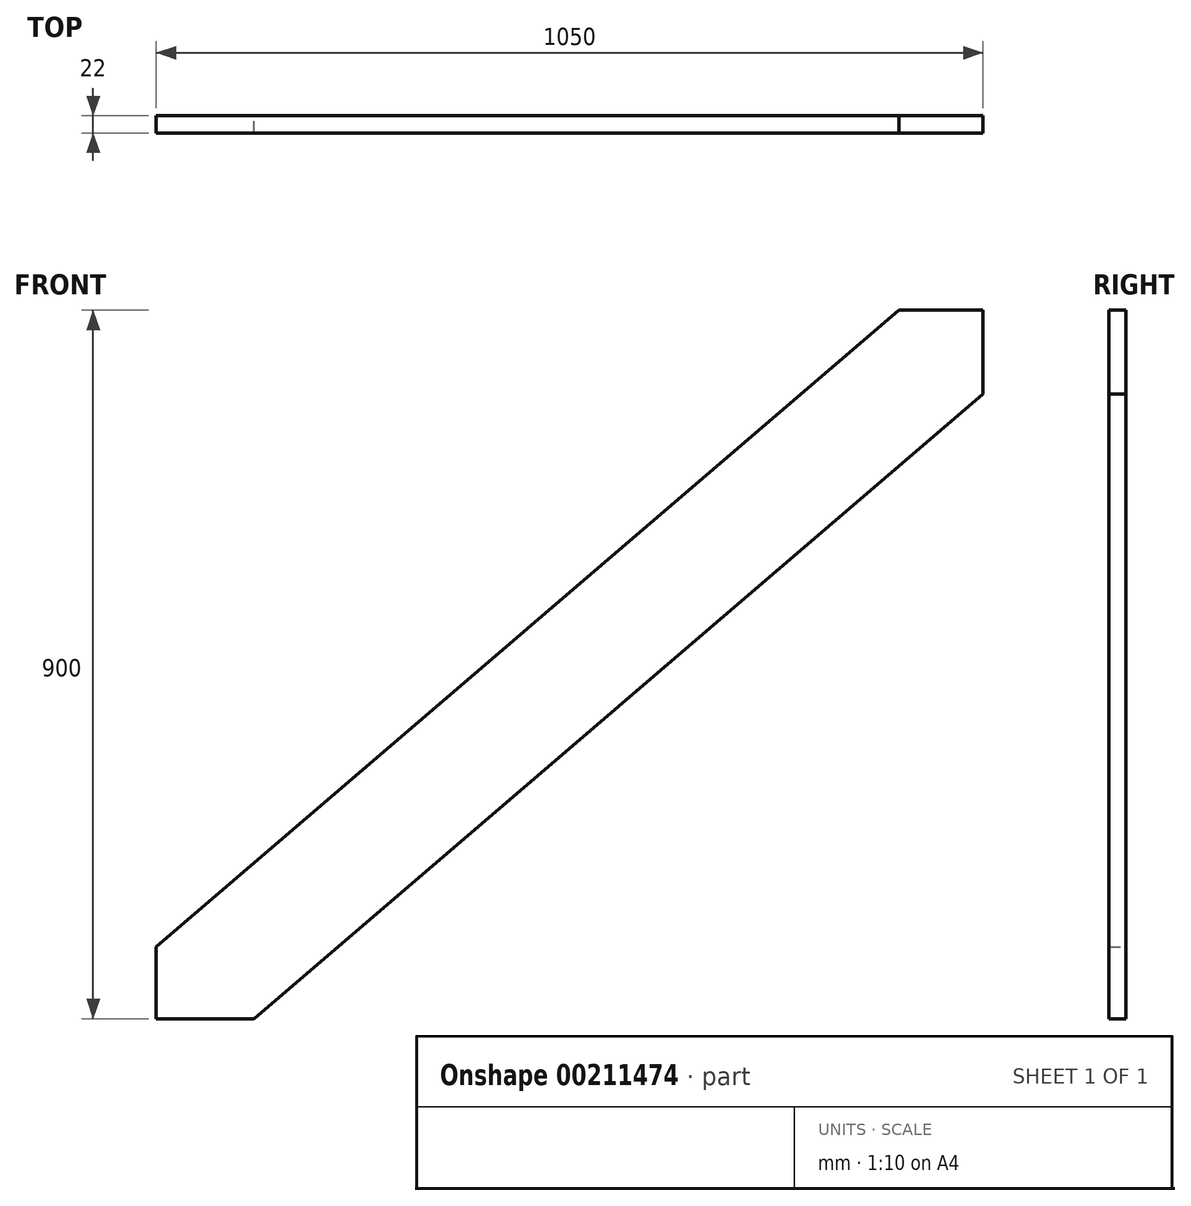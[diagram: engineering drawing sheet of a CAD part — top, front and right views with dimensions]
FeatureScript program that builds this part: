
annotation { "Feature Type Name" : "Feature", "Feature Type Description" : "" }
export const myFeature = defineFeature(function(context is Context, id is Id, definition is map)
    precondition{}
    {
        {
            var Q0;
            Q0=qCreatedBy(makeId("Front.planeOp"),FACE);
            var sketch = newSketch(context, id + "F0", { "sketchPlane" : qUnion([Q0])});
            skLineSegment(sketch, "E0.bottom", {"start": v(-525, 450) * mm, "end": v(525, 450) * mm, "construction": true});
            skLineSegment(sketch, "E0.top", {"start": v(-525, -450) * mm, "end": v(525, -450) * mm, "construction": true});
            skLineSegment(sketch, "E0.left", {"start": v(-525, 450) * mm, "end": v(-525, -450) * mm, "construction": true});
            skLineSegment(sketch, "E0.right", {"start": v(525, 450) * mm, "end": v(525, -450) * mm, "construction": true});
            skLineSegment(sketch, "E1", {"start": v(0, 0) * mm, "end": v(525, 450) * mm, "construction": true});
            skLineSegment(sketch, "E2", {"start": v(418.62, 450) * mm, "end": v(-525, -358.82) * mm});
            skLineSegment(sketch, "E3", {"start": v(-525, -358.82) * mm, "end": v(-525, -450) * mm});
            skLineSegment(sketch, "E4", {"start": v(418.62, 450) * mm, "end": v(525, 450) * mm});
            skLineSegment(sketch, "E5", {"start": v(525, 343.62) * mm, "end": v(-400.9, -450) * mm});
            skLineSegment(sketch, "E6", {"start": v(-400.9, -450) * mm, "end": v(-525, -450) * mm});
            skLineSegment(sketch, "E7", {"start": v(525, 343.62) * mm, "end": v(525, 450) * mm});
            skSolve(sketch);
        }
        {
            var Q0;
            Q0 = qSketchRegion(id + "F0", true);
            extrude(context, id + "F1", {"entities" : qUnion([Q0]), "depth" : 22 * mm});
        }
    });
